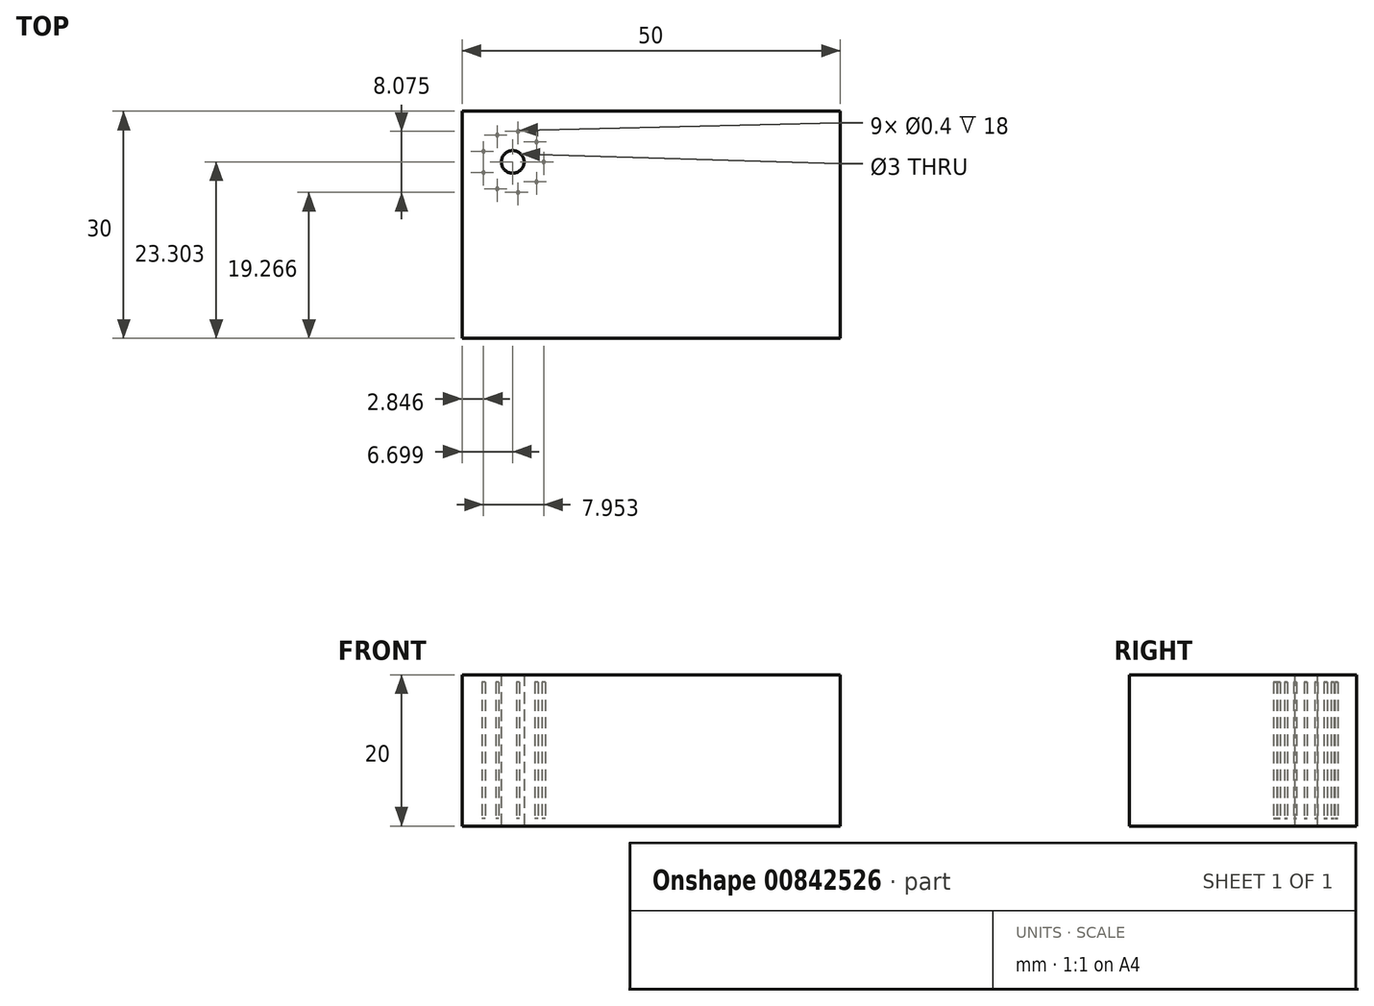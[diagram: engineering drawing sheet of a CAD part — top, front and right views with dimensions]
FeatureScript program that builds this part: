
annotation { "Feature Type Name" : "Feature", "Feature Type Description" : "" }
export const myFeature = defineFeature(function(context is Context, id is Id, definition is map)
    precondition{}
    {
        {
            var Q0;
            Q0=qCreatedBy(makeId("Top.planeOp"),FACE);
            var Q1;
            Q1=qCreatedBy(makeId("Top.planeOp"),FACE);
            var Q2;
            Q2=qCreatedBy(makeId("Top.planeOp"),FACE);
            var sketch = newSketch(context, id + "F0", { "sketchPlane" : qUnion([Q0, Q1, Q2])});
            skLineSegment(sketch, "E0.bottom", {"start": v(22.94, -4.42) * mm, "end": v(72.94, -4.42) * mm});
            skLineSegment(sketch, "E0.top", {"start": v(22.94, -34.42) * mm, "end": v(72.94, -34.42) * mm});
            skLineSegment(sketch, "E0.left", {"start": v(22.94, -4.42) * mm, "end": v(22.94, -34.42) * mm});
            skLineSegment(sketch, "E0.right", {"start": v(72.94, -4.42) * mm, "end": v(72.94, -34.42) * mm});
            skSolve(sketch);
        }
        {
            var Q0;
            Q0=makeQuery(id+"F0.imprint","IMPRINT",FACE,{"disambiguationData":[TD([[makeQuery(id+"F0.imprint","IMPRINT",EDGE,{"derivedFrom":sQuery(id+"F0.wireOp",EDGE,"E0.bottom")}),-1.0]])]});
            extrude(context, id + "F1", {"entities" : qUnion([Q0]), "endBound" : BoundingType.SYMMETRIC, "depth" : 20 * mm, "offsetDistance" : 25 * mm});
        }
        {
            var Q0;
            Q0=qCreatedBy(makeId("Top.planeOp"),FACE);
            var sketch = newSketch(context, id + "F2", { "sketchPlane" : qUnion([Q0])});
            skCircle(sketch, "E1", {"center": v(29.64, -11.12) * mm, "radius": 1.5 * mm});
            skCircle(sketch, "E2", {"center": v(33.74, -11.12) * mm, "radius": 0.2 * mm});
            skLineSegment(sketch, "E3", {"start": v(29.64, -11.12) * mm, "end": v(33.74, -11.12) * mm, "construction": true});
            skCircle(sketch, "E4", {"center": v(32.78, -8.48) * mm, "radius": 0.2 * mm, "construction": true});
            skLineSegment(sketch, "E5", {"start": v(29.64, -11.12) * mm, "end": v(32.78, -8.48) * mm, "construction": true});
            skCircle(sketch, "E6.1.0", {"center": v(32.78, -8.48) * mm, "radius": 0.2 * mm});
            skCircle(sketch, "E6.2.0", {"center": v(30.35, -7.08) * mm, "radius": 0.2 * mm});
            skCircle(sketch, "E6.3.0", {"center": v(27.59, -7.57) * mm, "radius": 0.2 * mm});
            skCircle(sketch, "E6.4.0", {"center": v(25.79, -9.71) * mm, "radius": 0.2 * mm});
            skCircle(sketch, "E6.5.0", {"center": v(25.79, -12.52) * mm, "radius": 0.2 * mm});
            skCircle(sketch, "E6.6.0", {"center": v(27.59, -14.67) * mm, "radius": 0.2 * mm});
            skCircle(sketch, "E6.7.0", {"center": v(30.35, -15.15) * mm, "radius": 0.2 * mm});
            skCircle(sketch, "E7.1.8.0", {"center": v(32.78, -13.75) * mm, "radius": 0.2 * mm});
            skSolve(sketch);
        }
        {
            var Q0;
            Q0 = qSketchRegion(id + "F2", true);
            extrude(context, id + "F3", {"entities" : qUnion([Q0]), "operationType" : NewBodyOperationType.REMOVE, "endBound" : BoundingType.SYMMETRIC, "depth" : 18 * mm, "offsetDistance" : 25 * mm});
        }
        {
            var Q0;
            Q0=makeQuery(id+"F2.imprint","IMPRINT",FACE,{"disambiguationData":[TD([[makeQuery(id+"F2.imprint","IMPRINT",EDGE,{"derivedFrom":sQuery(id+"F2.wireOp",EDGE,"E1")}),1.0]])]});
            extrude(context, id + "F4", {"entities" : qUnion([Q0]), "operationType" : NewBodyOperationType.REMOVE, "endBound" : BoundingType.SYMMETRIC, "oppositeDirection" : true, "depth" : 25 * mm, "offsetDistance" : 25 * mm});
        }
    });
